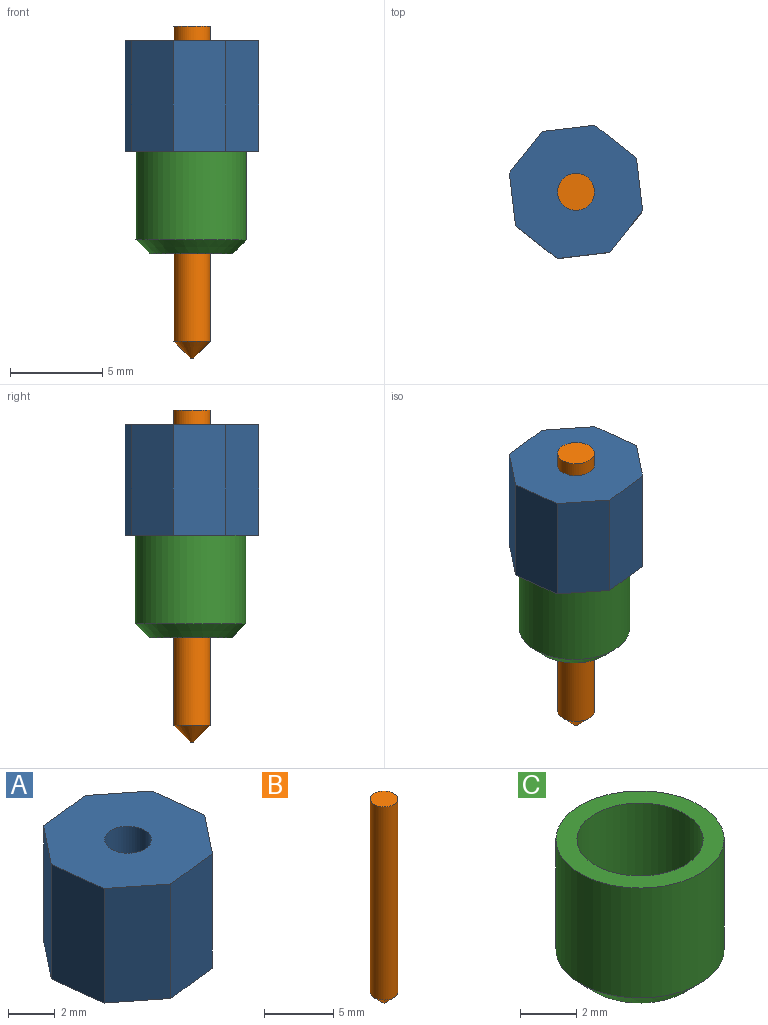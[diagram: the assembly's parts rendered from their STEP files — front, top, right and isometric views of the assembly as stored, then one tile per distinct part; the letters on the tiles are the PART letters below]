
ASSEMBLY  parts=3 mates=2
PART A: 11 faces, bbox 7.2x7.2x6 mm
  f0: plane 6x2.85mm, normal (0.12,-0.99,0), area 17.2mm2, adj f1,f7,f9,f10
  f1: plane 6x2.25mm, normal (0.78,-0.62,0), area 17.2mm2, adj f0,f2,f9,f10
  f2: plane 6x2.85mm, normal (0.99,0.12,0), area 17.2mm2, adj f1,f3,f9,f10
  f3: plane 6x2.25mm, normal (0.62,0.78,0), area 17.2mm2, adj f2,f4,f9,f10
  f4: plane 6x2.85mm, normal (-0.12,0.99,0), area 17.2mm2, adj f3,f5,f9,f10
  f5: plane 6x2.25mm, normal (-0.78,0.62,0), area 17.2mm2, adj f4,f6,f9,f10
  f6: plane 6x2.85mm, normal (-0.99,-0.12,0), area 17.2mm2, adj f5,f7,f9,f10
  f7: plane 6x2.25mm, normal (-0.62,-0.78,0), area 17.2mm2, adj f0,f6,f9,f10
  f8: cylinder r=1mm len=6mm, axis (0,0,-1), area 37.7mm2, adj f9,f10
  f9: plane 7.22x7.22mm, normal (0,0,1), area 36.7mm2, adj f0,f1,f2,f3,f4,f5,f6,f7
  f10: plane 7.22x7.22mm, normal (0,0,-1), area 36.7mm2, adj f0,f1,f2,f3,f4,f5,f6,f7
PART B: 4 faces, bbox 2x2x18 mm
  f0: cylinder r=1mm len=17.1mm, axis (0,0,-1), area 107.4mm2, adj f1,f3
  f1: plane 2x2mm, normal (0,0,1), area 3.1mm2, adj f0
  f2: plane 0.2x0.2mm, normal (0,0,-1), area 0mm2, adj f3
  f3: cone r=1mm half-angle=45deg, axis (0,0,1), area 4.4mm2, adj f0,f2
PART C: 4 faces, bbox 6x6x5.6 mm
  f0: cylinder r=2.25mm len=5.55mm, axis (0,0,-1), area 78.5mm2, adj f2,f3
  f1: cylinder r=3mm len=6mm, axis (0,0,-1), area 90.5mm2, adj f2,f3
  f2: plane 6x6mm, normal (0,0,1), area 12.4mm2, adj f0,f1
  f3: cone r=3mm half-angle=45deg, axis (0,0,1), area 17.5mm2, adj f0,f1
PLACE A t=(14.29,-17,5.77)mm
PLACE B t=(15.29,-32.67,-5.43)mm
PLACE C t=(15.24,-6.61,-0.23)mm
MATE slider B.f0 <-> A.f8  axis (0,0,-1) through (-15.96,-4.8,4.02)mm
MATE planar C.f0 <-> A.f8  axis (0,0,1) through (-16,-4.72,5.77)mm
